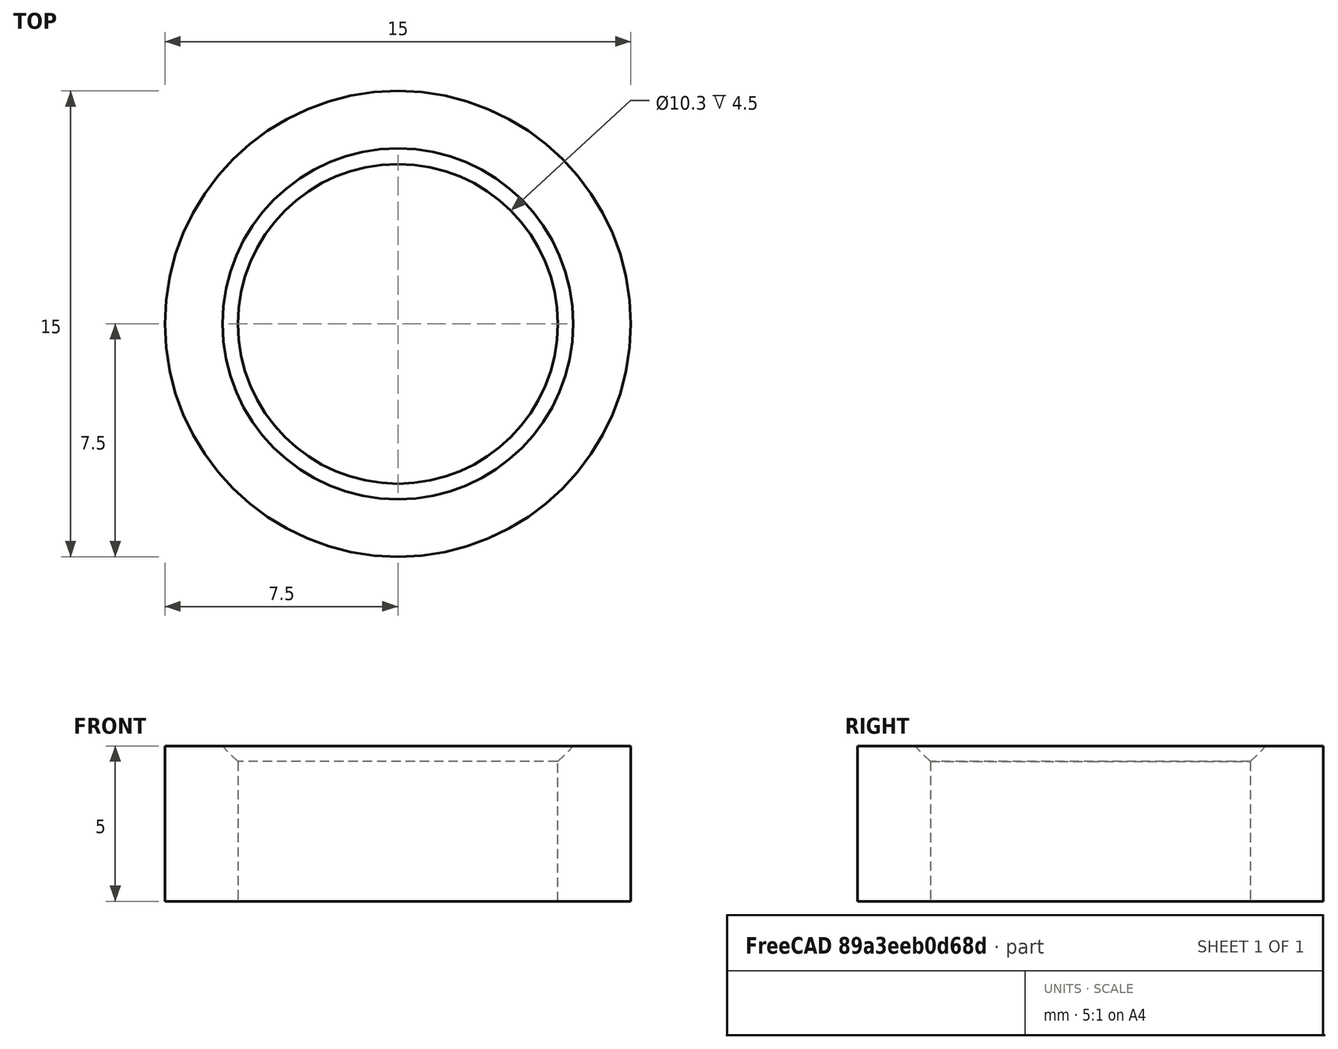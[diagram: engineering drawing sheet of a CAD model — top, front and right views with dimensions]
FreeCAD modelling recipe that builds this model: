
FCSTD DOCUMENT  (FreeCAD 0.19R24276 (Git))
Label: b_fix_part_3
License: All rights reserved
LicenseURL: http://en.wikipedia.org/wiki/All_rights_reserved
objects: Sketcher::SketchObject×1, PartDesign::Pad×1, PartDesign::Chamfer×1, PartDesign::Body×1
note: 6 computed .brp shape members not serialized (recipe doc carries the construction recipe); baked Part::Feature solids carry a one-line shape summary decoded from their .brp

FEATURE [Sketcher::SketchObject] Sketch
  FullyConstrained = true
  MapMode = 5
  Support = -> [XY_Plane]
  sketch-geometry (2):
    g0: Circle CenterX=0 CenterY=0 CenterZ=0 NormalX=0 NormalY=0 NormalZ=1 AngleXU=0 Radius=5.15
    g1: Circle CenterX=0 CenterY=0 CenterZ=0 NormalX=0 NormalY=0 NormalZ=1 AngleXU=0 Radius=7.5
  constraints (4):
    c: Coincident(g0,g-1)
    c: Diameter(g0) = 10.3
    c: Coincident(g1,g0)
    c: Diameter(g1) = 15
FEATURE [PartDesign::Pad] Pad
  Direction = (1,1,1)
  Length = 5
  Length2 = 100
  Profile = -> Sketch
  Type = 0
FEATURE [PartDesign::Chamfer] Chamfer
  Angle = 45
  Base = -> Pad [Edge6]
  BaseFeature = -> Pad
  ChamferType = 0
  FlipDirection = false
  Size = 0.5
  Size2 = 1
  SupportTransform = false
FEATURE [PartDesign::Body] Body
  Group = -> [Sketch,Pad,Chamfer]
  Origin = -> Origin
  Tip = -> Chamfer
